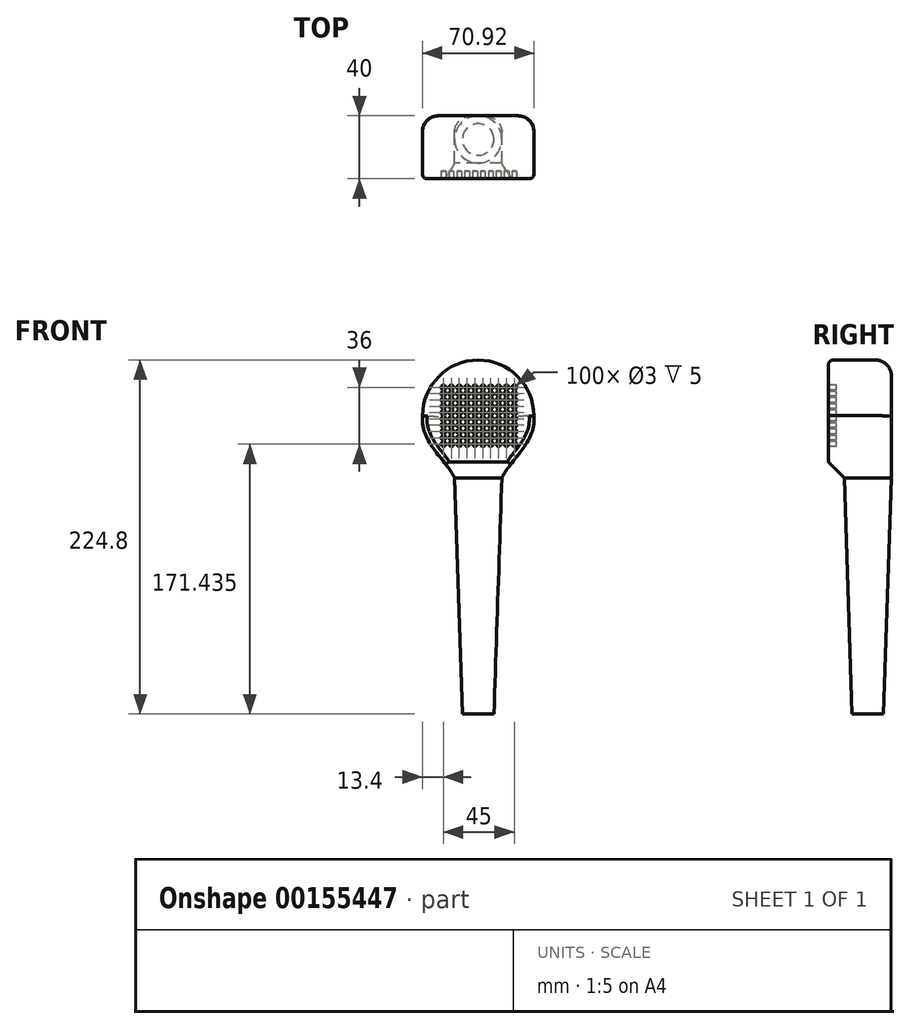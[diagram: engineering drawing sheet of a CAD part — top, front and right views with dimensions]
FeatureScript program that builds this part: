
annotation { "Feature Type Name" : "Feature", "Feature Type Description" : "" }
export const myFeature = defineFeature(function(context is Context, id is Id, definition is map)
    precondition{}
    {
        {
            var Q0;
            Q0=qCreatedBy(makeId("Top.planeOp"),FACE);
            var sketch = newSketch(context, id + "F0", { "sketchPlane" : qUnion([Q0])});
            skCircle(sketch, "E0", {"center": v(0, 0) * mm, "radius": 10 * mm});
            skSolve(sketch);
        }
        {
            var Q0;
            Q0=qCreatedBy(makeId("Top.planeOp"),FACE);
            cPlane(context, id + "F1", {"entities" : qUnion([Q0]), "cplaneType" : CPlaneType.OFFSET, "offset" : 150 * mm, "width" : 150 * mm, "height" : 150 * mm});
        }
        {
            var Q0;
            Q0=qCreatedBy(id+"F1.planeOp",FACE);
            var sketch = newSketch(context, id + "F2", { "sketchPlane" : qUnion([Q0])});
            skCircle(sketch, "E1", {"center": v(0, 0) * mm, "radius": 15 * mm});
            skSolve(sketch);
        }
        {
            var Q0;
            Q0=makeQuery(id+"F0.imprint","IMPRINT",FACE,{"disambiguationData":[TD([[makeQuery(id+"F0.imprint","IMPRINT",EDGE,{"derivedFrom":sQuery(id+"F0.wireOp",EDGE,"E0")}),1.0]])]});
            var Q1;
            Q1=makeQuery(id+"F2.imprint","IMPRINT",FACE,{"disambiguationData":[TD([[makeQuery(id+"F2.imprint","IMPRINT",EDGE,{"derivedFrom":sQuery(id+"F2.wireOp",EDGE,"E1")}),1.0]])]});
            loft(context, id + "F3", {"sheetProfilesArray" : [{ "sheetProfileEntities" : qUnion([Q0]) }, { "sheetProfileEntities" : qUnion([Q1]) }]});
        }
        {
            var Q0;
            Q0=qCreatedBy(makeId("Front.planeOp"),FACE);
            var sketch = newSketch(context, id + "F4", { "sketchPlane" : qUnion([Q0])});
            skArc(sketch, "E2", {"start": v(35.32, 189.48) * mm, "mid": v(0, 224.8) * mm, "end": v(-35.32, 189.48) * mm});
            skLineSegment(sketch, "E3.0", {"start": v(-15, 150) * mm, "end": v(15, 150) * mm});
            skLineSegment(sketch, "E4", {"start": v(0, 150) * mm, "end": v(0, 162.36) * mm, "construction": true});
            skPoint(sketch, "E4.endSnap0", {"position": v(0, 150) * mm});
            skLineSegment(sketch, "E5", {"start": v(0, 189.48) * mm, "end": v(35.32, 189.48) * mm, "construction": true});
            skFitSpline(sketch, "E6", {"points": [v(-35.32, 189.48) * mm, v(-15, 150) * mm], "startDerivative": vector(-5.24, -48.94) * mm, "endDerivative": vector(20.32, -39.48) * mm});
            skFitSpline(sketch, "E7.MirrorCS", {"points": [v(35.32, 189.48) * mm, v(15, 150) * mm], "startDerivative": vector(5.24, -48.94) * mm, "endDerivative": vector(-20.32, -39.48) * mm});
            skSolve(sketch);
        }
        {
            var Q0;
            Q0=makeQuery(id+"F4.imprint","IMPRINT",FACE,{"disambiguationData":[TD([[makeQuery(id+"F4.imprint","IMPRINT",EDGE,{"derivedFrom":sQuery(id+"F4.wireOp",EDGE,"E2")}),1.0]])]});
            extrude(context, id + "F5", {"entities" : qUnion([Q0]), "operationType" : NewBodyOperationType.ADD, "endBound" : BoundingType.SYMMETRIC, "depth" : 30 * mm});
        }
        {
            var Q0;
            Q0=makeQuery(id+"F5.opExtrude","CAP_EDGE",EDGE,{"disambiguationData":[OSD([sQuery(id+"F4.wireOp",EDGE,"E2")])],"isStart":true});
            var Q1;
            Q1=makeQuery(id+"F5.opExtrude","CAP_EDGE",EDGE,{"disambiguationData":[OSD([sQuery(id+"F4.wireOp",EDGE,"E7.MirrorCS")])],"isStart":true});
            var Q2;
            Q2=makeQuery(id+"F5.opExtrude","CAP_EDGE",EDGE,{"disambiguationData":[OSD([sQuery(id+"F4.wireOp",EDGE,"E6")])],"isStart":true});
            fillet(context, id + "F6", {"entities" : qUnion([Q0, Q1, Q2]), "radius" : 10 * mm, "tangentPropagation" : true, "allowEdgeOverflow" : false});
        }
        {
            var Q0;
            Q0=makeQuery(id+"F5.opExtrude","CAP_FACE",FACE,{"disambiguationData":[OSD([sQuery(id+"F4.wireOp",EDGE,"E2"),sQuery(id+"F4.wireOp",EDGE,"E3.0"),sQuery(id+"F4.wireOp",EDGE,"E6"),sQuery(id+"F4.wireOp",EDGE,"E7.MirrorCS")])],"isStart":false});
            extrude(context, id + "F7", {"entities" : qUnion([Q0]), "operationType" : NewBodyOperationType.ADD, "depth" : 10 * mm});
        }
        {
            var Q0;
            Q0=makeQuery(id+"F7.opExtrude","CAP_FACE",FACE,{"disambiguationData":[OSD([sQuery(id+"F4.wireOp",EDGE,"E2"),sQuery(id+"F4.wireOp",EDGE,"E3.0"),sQuery(id+"F4.wireOp",EDGE,"E6"),sQuery(id+"F4.wireOp",EDGE,"E7.MirrorCS")])],"isStart":false});
            var sketch = newSketch(context, id + "F8", { "sketchPlane" : qUnion([Q0])});
            skCircle(sketch, "E8", {"center": v(-22.06, 171.43) * mm, "radius": 1.5 * mm});
            skCircle(sketch, "E9.0.1.0", {"center": v(-22.06, 175.43) * mm, "radius": 1.5 * mm});
            skCircle(sketch, "E9.0.2.0", {"center": v(-22.06, 179.43) * mm, "radius": 1.5 * mm});
            skCircle(sketch, "E9.0.3.0", {"center": v(-22.06, 183.43) * mm, "radius": 1.5 * mm});
            skCircle(sketch, "E9.0.4.0", {"center": v(-22.06, 187.43) * mm, "radius": 1.5 * mm});
            skCircle(sketch, "E9.0.5.0", {"center": v(-22.06, 191.43) * mm, "radius": 1.5 * mm});
            skCircle(sketch, "E9.0.6.0", {"center": v(-22.06, 195.43) * mm, "radius": 1.5 * mm});
            skCircle(sketch, "E9.0.7.0", {"center": v(-22.06, 199.43) * mm, "radius": 1.5 * mm});
            skCircle(sketch, "E9.0.8.0", {"center": v(-22.06, 203.43) * mm, "radius": 1.5 * mm});
            skCircle(sketch, "E9.0.9.0", {"center": v(-22.06, 207.43) * mm, "radius": 1.5 * mm});
            skCircle(sketch, "E9.1.0.0", {"center": v(-17.06, 171.43) * mm, "radius": 1.5 * mm});
            skCircle(sketch, "E9.1.1.0", {"center": v(-17.06, 175.43) * mm, "radius": 1.5 * mm});
            skCircle(sketch, "E9.1.2.0", {"center": v(-17.06, 179.43) * mm, "radius": 1.5 * mm});
            skCircle(sketch, "E9.1.3.0", {"center": v(-17.06, 183.43) * mm, "radius": 1.5 * mm});
            skCircle(sketch, "E9.1.4.0", {"center": v(-17.06, 187.43) * mm, "radius": 1.5 * mm});
            skCircle(sketch, "E9.1.5.0", {"center": v(-17.06, 191.43) * mm, "radius": 1.5 * mm});
            skCircle(sketch, "E9.1.6.0", {"center": v(-17.06, 195.43) * mm, "radius": 1.5 * mm});
            skCircle(sketch, "E9.1.7.0", {"center": v(-17.06, 199.43) * mm, "radius": 1.5 * mm});
            skCircle(sketch, "E9.1.8.0", {"center": v(-17.06, 203.43) * mm, "radius": 1.5 * mm});
            skCircle(sketch, "E9.1.9.0", {"center": v(-17.06, 207.43) * mm, "radius": 1.5 * mm});
            skCircle(sketch, "E9.2.0.0", {"center": v(-12.06, 171.43) * mm, "radius": 1.5 * mm});
            skCircle(sketch, "E9.2.1.0", {"center": v(-12.06, 175.43) * mm, "radius": 1.5 * mm});
            skCircle(sketch, "E9.2.2.0", {"center": v(-12.06, 179.43) * mm, "radius": 1.5 * mm});
            skCircle(sketch, "E9.2.3.0", {"center": v(-12.06, 183.43) * mm, "radius": 1.5 * mm});
            skCircle(sketch, "E9.2.4.0", {"center": v(-12.06, 187.43) * mm, "radius": 1.5 * mm});
            skCircle(sketch, "E9.2.5.0", {"center": v(-12.06, 191.43) * mm, "radius": 1.5 * mm});
            skCircle(sketch, "E9.2.6.0", {"center": v(-12.06, 195.43) * mm, "radius": 1.5 * mm});
            skCircle(sketch, "E9.2.7.0", {"center": v(-12.06, 199.43) * mm, "radius": 1.5 * mm});
            skCircle(sketch, "E9.2.8.0", {"center": v(-12.06, 203.43) * mm, "radius": 1.5 * mm});
            skCircle(sketch, "E9.2.9.0", {"center": v(-12.06, 207.43) * mm, "radius": 1.5 * mm});
            skCircle(sketch, "E9.3.0.0", {"center": v(-7.06, 171.43) * mm, "radius": 1.5 * mm});
            skCircle(sketch, "E9.3.1.0", {"center": v(-7.06, 175.43) * mm, "radius": 1.5 * mm});
            skCircle(sketch, "E9.3.2.0", {"center": v(-7.06, 179.43) * mm, "radius": 1.5 * mm});
            skCircle(sketch, "E9.3.3.0", {"center": v(-7.06, 183.43) * mm, "radius": 1.5 * mm});
            skCircle(sketch, "E9.3.4.0", {"center": v(-7.06, 187.43) * mm, "radius": 1.5 * mm});
            skCircle(sketch, "E9.3.5.0", {"center": v(-7.06, 191.43) * mm, "radius": 1.5 * mm});
            skCircle(sketch, "E9.3.6.0", {"center": v(-7.06, 195.43) * mm, "radius": 1.5 * mm});
            skCircle(sketch, "E9.3.7.0", {"center": v(-7.06, 199.43) * mm, "radius": 1.5 * mm});
            skCircle(sketch, "E9.3.8.0", {"center": v(-7.06, 203.43) * mm, "radius": 1.5 * mm});
            skCircle(sketch, "E9.3.9.0", {"center": v(-7.06, 207.43) * mm, "radius": 1.5 * mm});
            skCircle(sketch, "E9.4.0.0", {"center": v(-2.06, 171.43) * mm, "radius": 1.5 * mm});
            skCircle(sketch, "E9.4.1.0", {"center": v(-2.06, 175.43) * mm, "radius": 1.5 * mm});
            skCircle(sketch, "E9.4.2.0", {"center": v(-2.06, 179.43) * mm, "radius": 1.5 * mm});
            skCircle(sketch, "E9.4.3.0", {"center": v(-2.06, 183.43) * mm, "radius": 1.5 * mm});
            skCircle(sketch, "E9.4.4.0", {"center": v(-2.06, 187.43) * mm, "radius": 1.5 * mm});
            skCircle(sketch, "E9.4.5.0", {"center": v(-2.06, 191.43) * mm, "radius": 1.5 * mm});
            skCircle(sketch, "E9.4.6.0", {"center": v(-2.06, 195.43) * mm, "radius": 1.5 * mm});
            skCircle(sketch, "E9.4.7.0", {"center": v(-2.06, 199.43) * mm, "radius": 1.5 * mm});
            skCircle(sketch, "E9.4.8.0", {"center": v(-2.06, 203.43) * mm, "radius": 1.5 * mm});
            skCircle(sketch, "E9.4.9.0", {"center": v(-2.06, 207.43) * mm, "radius": 1.5 * mm});
            skCircle(sketch, "E9.5.0.0", {"center": v(2.94, 171.43) * mm, "radius": 1.5 * mm});
            skCircle(sketch, "E9.5.1.0", {"center": v(2.94, 175.43) * mm, "radius": 1.5 * mm});
            skCircle(sketch, "E9.5.2.0", {"center": v(2.94, 179.43) * mm, "radius": 1.5 * mm});
            skCircle(sketch, "E9.5.3.0", {"center": v(2.94, 183.43) * mm, "radius": 1.5 * mm});
            skCircle(sketch, "E9.5.4.0", {"center": v(2.94, 187.43) * mm, "radius": 1.5 * mm});
            skCircle(sketch, "E9.5.5.0", {"center": v(2.94, 191.43) * mm, "radius": 1.5 * mm});
            skCircle(sketch, "E9.5.6.0", {"center": v(2.94, 195.43) * mm, "radius": 1.5 * mm});
            skCircle(sketch, "E9.5.7.0", {"center": v(2.94, 199.43) * mm, "radius": 1.5 * mm});
            skCircle(sketch, "E9.5.8.0", {"center": v(2.94, 203.43) * mm, "radius": 1.5 * mm});
            skCircle(sketch, "E9.5.9.0", {"center": v(2.94, 207.43) * mm, "radius": 1.5 * mm});
            skCircle(sketch, "E9.6.0.0", {"center": v(7.94, 171.43) * mm, "radius": 1.5 * mm});
            skCircle(sketch, "E9.6.1.0", {"center": v(7.94, 175.43) * mm, "radius": 1.5 * mm});
            skCircle(sketch, "E9.6.2.0", {"center": v(7.94, 179.43) * mm, "radius": 1.5 * mm});
            skCircle(sketch, "E9.6.3.0", {"center": v(7.94, 183.43) * mm, "radius": 1.5 * mm});
            skCircle(sketch, "E9.6.4.0", {"center": v(7.94, 187.43) * mm, "radius": 1.5 * mm});
            skCircle(sketch, "E9.6.5.0", {"center": v(7.94, 191.43) * mm, "radius": 1.5 * mm});
            skCircle(sketch, "E9.6.6.0", {"center": v(7.94, 195.43) * mm, "radius": 1.5 * mm});
            skCircle(sketch, "E9.6.7.0", {"center": v(7.94, 199.43) * mm, "radius": 1.5 * mm});
            skCircle(sketch, "E9.6.8.0", {"center": v(7.94, 203.43) * mm, "radius": 1.5 * mm});
            skCircle(sketch, "E9.6.9.0", {"center": v(7.94, 207.43) * mm, "radius": 1.5 * mm});
            skCircle(sketch, "E9.7.0.0", {"center": v(12.94, 171.43) * mm, "radius": 1.5 * mm});
            skCircle(sketch, "E9.7.1.0", {"center": v(12.94, 175.43) * mm, "radius": 1.5 * mm});
            skCircle(sketch, "E9.7.2.0", {"center": v(12.94, 179.43) * mm, "radius": 1.5 * mm});
            skCircle(sketch, "E9.7.3.0", {"center": v(12.94, 183.43) * mm, "radius": 1.5 * mm});
            skCircle(sketch, "E9.7.4.0", {"center": v(12.94, 187.43) * mm, "radius": 1.5 * mm});
            skCircle(sketch, "E9.7.5.0", {"center": v(12.94, 191.43) * mm, "radius": 1.5 * mm});
            skCircle(sketch, "E9.7.6.0", {"center": v(12.94, 195.43) * mm, "radius": 1.5 * mm});
            skCircle(sketch, "E9.7.7.0", {"center": v(12.94, 199.43) * mm, "radius": 1.5 * mm});
            skCircle(sketch, "E9.7.8.0", {"center": v(12.94, 203.43) * mm, "radius": 1.5 * mm});
            skCircle(sketch, "E9.7.9.0", {"center": v(12.94, 207.43) * mm, "radius": 1.5 * mm});
            skCircle(sketch, "E9.8.0.0", {"center": v(17.94, 171.43) * mm, "radius": 1.5 * mm});
            skCircle(sketch, "E9.8.1.0", {"center": v(17.94, 175.43) * mm, "radius": 1.5 * mm});
            skCircle(sketch, "E9.8.2.0", {"center": v(17.94, 179.43) * mm, "radius": 1.5 * mm});
            skCircle(sketch, "E9.8.3.0", {"center": v(17.94, 183.43) * mm, "radius": 1.5 * mm});
            skCircle(sketch, "E9.8.4.0", {"center": v(17.94, 187.43) * mm, "radius": 1.5 * mm});
            skCircle(sketch, "E9.8.5.0", {"center": v(17.94, 191.43) * mm, "radius": 1.5 * mm});
            skCircle(sketch, "E9.8.6.0", {"center": v(17.94, 195.43) * mm, "radius": 1.5 * mm});
            skCircle(sketch, "E9.8.7.0", {"center": v(17.94, 199.43) * mm, "radius": 1.5 * mm});
            skCircle(sketch, "E9.8.8.0", {"center": v(17.94, 203.43) * mm, "radius": 1.5 * mm});
            skCircle(sketch, "E9.8.9.0", {"center": v(17.94, 207.43) * mm, "radius": 1.5 * mm});
            skCircle(sketch, "E9.9.0.0", {"center": v(22.94, 171.43) * mm, "radius": 1.5 * mm});
            skCircle(sketch, "E9.9.1.0", {"center": v(22.94, 175.43) * mm, "radius": 1.5 * mm});
            skCircle(sketch, "E9.9.2.0", {"center": v(22.94, 179.43) * mm, "radius": 1.5 * mm});
            skCircle(sketch, "E9.9.3.0", {"center": v(22.94, 183.43) * mm, "radius": 1.5 * mm});
            skCircle(sketch, "E9.9.4.0", {"center": v(22.94, 187.43) * mm, "radius": 1.5 * mm});
            skCircle(sketch, "E9.9.5.0", {"center": v(22.94, 191.43) * mm, "radius": 1.5 * mm});
            skCircle(sketch, "E9.9.6.0", {"center": v(22.94, 195.43) * mm, "radius": 1.5 * mm});
            skCircle(sketch, "E9.9.7.0", {"center": v(22.94, 199.43) * mm, "radius": 1.5 * mm});
            skCircle(sketch, "E9.9.8.0", {"center": v(22.94, 203.43) * mm, "radius": 1.5 * mm});
            skCircle(sketch, "E9.9.9.0", {"center": v(22.94, 207.43) * mm, "radius": 1.5 * mm});
            skLineSegment(sketch, "E9.direction1", {"start": v(-22.06, 171.43) * mm, "end": v(-17.06, 171.43) * mm, "construction": true});
            skLineSegment(sketch, "E9.direction2", {"start": v(-22.06, 171.43) * mm, "end": v(-22.06, 175.43) * mm, "construction": true});
            skSolve(sketch);
        }
        {
            var Q0;
            Q0 = qSketchRegion(id + "F8", true);
            extrude(context, id + "F9", {"entities" : qUnion([Q0]), "operationType" : NewBodyOperationType.REMOVE, "oppositeDirection" : true, "depth" : 5 * mm});
        }
        {
            var Q0;
            Q0=makeQuery(id+"F7.opExtrude","CAP_EDGE",EDGE,{"disambiguationData":[OSD([sQuery(id+"F4.wireOp",EDGE,"E3.0")])],"isStart":false});
            chamfer(context, id + "F10", {"entities" : qUnion([Q0]), "width" : 10 * mm, "tangentPropagation" : true});
        }
        {
            var Q0;
            Q0=makeQuery(id+"F7.opExtrude","CAP_EDGE",EDGE,{"disambiguationData":[OSD([sQuery(id+"F4.wireOp",EDGE,"E6")])],"isStart":false});
            var Q1;
            Q1=makeQuery(id+"F7.opExtrude","CAP_EDGE",EDGE,{"disambiguationData":[OSD([sQuery(id+"F4.wireOp",EDGE,"E2")])],"isStart":false});
            var Q2;
            Q2=makeQuery(id+"F7.opExtrude","CAP_EDGE",EDGE,{"disambiguationData":[OSD([sQuery(id+"F4.wireOp",EDGE,"E7.MirrorCS")])],"isStart":false});
            fillet(context, id + "F11", {"entities" : qUnion([Q0, Q1, Q2]), "radius" : 3 * mm, "tangentPropagation" : true, "allowEdgeOverflow" : false});
        }
    });
